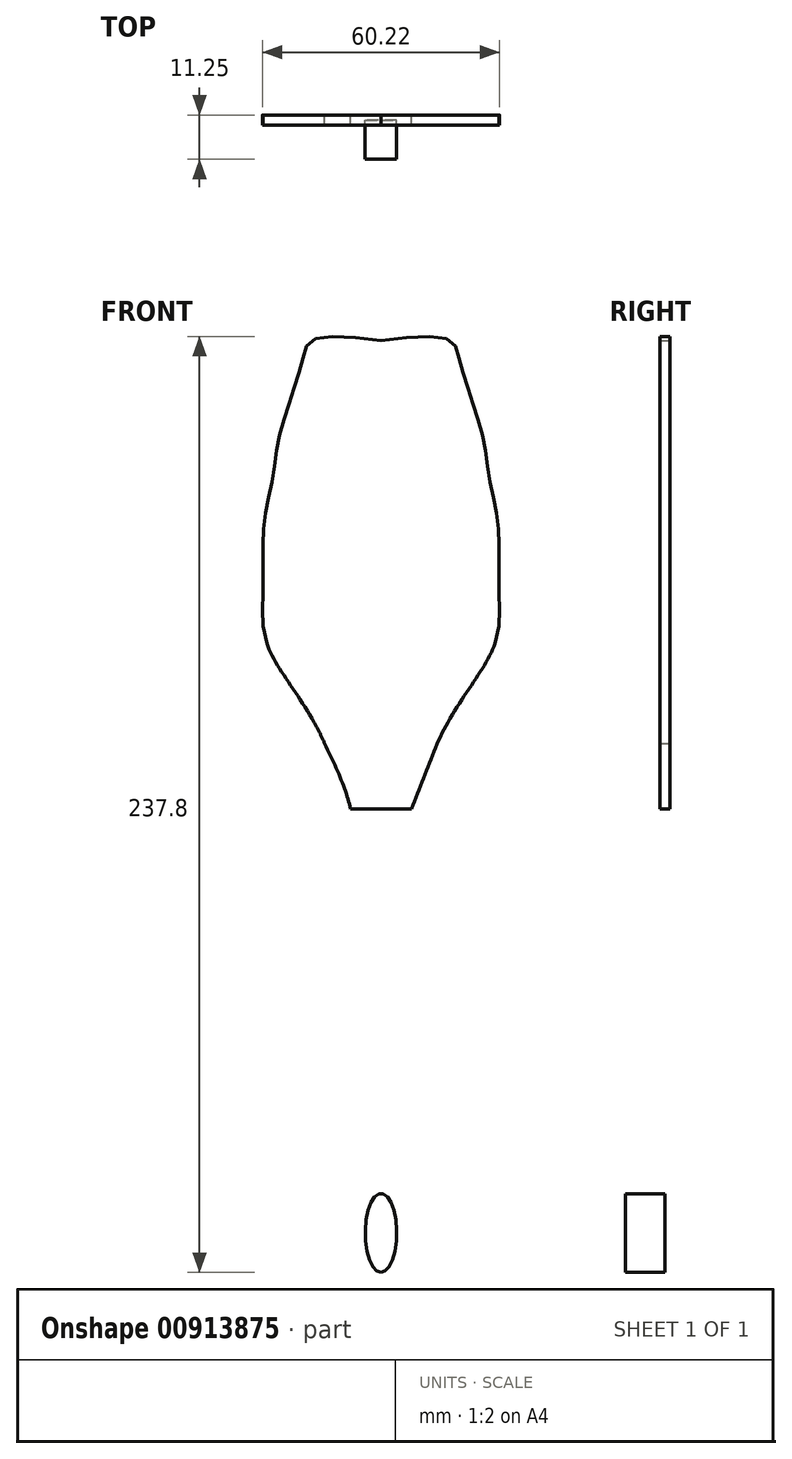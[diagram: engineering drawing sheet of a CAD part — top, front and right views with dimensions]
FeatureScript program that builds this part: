
annotation { "Feature Type Name" : "Feature", "Feature Type Description" : "" }
export const myFeature = defineFeature(function(context is Context, id is Id, definition is map)
    precondition{}
    {
        {
            var Q0;
            Q0=qCreatedBy(makeId("Front.planeOp"),FACE);
            var sketch = newSketch(context, id + "F0", { "sketchPlane" : qUnion([Q0])});
            skLineSegment(sketch, "E0", {"start": v(0, 0) * mm, "end": v(0, 20) * mm});
            skLineSegment(sketch, "E1", {"start": v(0, 20) * mm, "end": v(0, 22) * mm});
            skLineSegment(sketch, "E2", {"start": v(0, 22) * mm, "end": v(0, 32) * mm});
            skLineSegment(sketch, "E3", {"start": v(0, 32) * mm, "end": v(0, 42) * mm});
            skLineSegment(sketch, "E4", {"start": v(0, 42) * mm, "end": v(0, 52) * mm});
            skLineSegment(sketch, "E5", {"start": v(0, 52) * mm, "end": v(0, 62) * mm});
            skLineSegment(sketch, "E6", {"start": v(0, 62) * mm, "end": v(0, 72) * mm});
            skLineSegment(sketch, "E7", {"start": v(0, 72) * mm, "end": v(0, 82) * mm});
            skLineSegment(sketch, "E8", {"start": v(0, 82) * mm, "end": v(0, 92) * mm});
            skLineSegment(sketch, "E9", {"start": v(0, 92) * mm, "end": v(0, 97) * mm});
            skLineSegment(sketch, "E10", {"start": v(0, 20) * mm, "end": v(-29, 20) * mm, "construction": true});
            skLineSegment(sketch, "E11", {"start": v(0, 22) * mm, "end": v(-30, 22) * mm, "construction": true});
            skLineSegment(sketch, "E12", {"start": v(0, 32) * mm, "end": v(-30, 31.34) * mm, "construction": true});
            skLineSegment(sketch, "E13", {"start": v(0, 42) * mm, "end": v(-30, 42) * mm, "construction": true});
            skLineSegment(sketch, "E14", {"start": v(0, 52) * mm, "end": v(-29.5, 52) * mm, "construction": true});
            skLineSegment(sketch, "E15", {"start": v(0, 62) * mm, "end": v(-27.5, 62) * mm, "construction": true});
            skLineSegment(sketch, "E16", {"start": v(0, 72) * mm, "end": v(-26, 72) * mm, "construction": true});
            skLineSegment(sketch, "E17", {"start": v(0, 82) * mm, "end": v(-23, 82) * mm, "construction": true});
            skLineSegment(sketch, "E18", {"start": v(0, 92) * mm, "end": v(-20, 92) * mm, "construction": true});
            skLineSegment(sketch, "E19", {"start": v(0, 97) * mm, "end": v(-17.5, 97) * mm, "construction": true});
            skLineSegment(sketch, "E20", {"start": v(0, 0) * mm, "end": v(0, -22) * mm, "construction": true});
            skLineSegment(sketch, "E21", {"start": v(0, -22) * mm, "end": v(-7.75, -22) * mm});
            skLineSegment(sketch, "E22", {"start": v(0, -22) * mm, "end": v(0, -32) * mm, "construction": true});
            skLineSegment(sketch, "E23", {"start": v(0, -32) * mm, "end": v(0, -42) * mm, "construction": true});
            skLineSegment(sketch, "E24", {"start": v(0, -42) * mm, "end": v(0, -52) * mm, "construction": true});
            skLineSegment(sketch, "E25", {"start": v(0, -52) * mm, "end": v(0, -62) * mm, "construction": true});
            skLineSegment(sketch, "E26", {"start": v(0, -62) * mm, "end": v(0, -72) * mm, "construction": true});
            skLineSegment(sketch, "E27", {"start": v(0, -72) * mm, "end": v(0, -82) * mm, "construction": true});
            skLineSegment(sketch, "E28", {"start": v(0, -82) * mm, "end": v(0, -92) * mm, "construction": true});
            skLineSegment(sketch, "E29", {"start": v(0, -92) * mm, "end": v(0, -102) * mm, "construction": true});
            skLineSegment(sketch, "E30", {"start": v(0, -102) * mm, "end": v(0, -112) * mm, "construction": true});
            skLineSegment(sketch, "E31", {"start": v(0, -112) * mm, "end": v(0, -122) * mm, "construction": true});
            skLineSegment(sketch, "E32", {"start": v(0, -122) * mm, "end": v(0, -132) * mm, "construction": true});
            skLineSegment(sketch, "E33", {"start": v(0, -132) * mm, "end": v(0, -142) * mm, "construction": true});
            skLineSegment(sketch, "E34", {"start": v(0, -142) * mm, "end": v(0, -152) * mm, "construction": true});
            skLineSegment(sketch, "E35", {"start": v(0, -32) * mm, "end": v(-7.5, -32) * mm, "construction": true});
            skLineSegment(sketch, "E36", {"start": v(0, -42) * mm, "end": v(-7.6, -42) * mm, "construction": true});
            skLineSegment(sketch, "E37", {"start": v(0, -52) * mm, "end": v(-7.9, -52) * mm, "construction": true});
            skLineSegment(sketch, "E38", {"start": v(0, -62) * mm, "end": v(-8.4, -62) * mm, "construction": true});
            skLineSegment(sketch, "E39", {"start": v(0, -72) * mm, "end": v(-9, -72) * mm, "construction": true});
            skLineSegment(sketch, "E40", {"start": v(0, -82) * mm, "end": v(-10, -82) * mm, "construction": true});
            skLineSegment(sketch, "E41", {"start": v(0, -92) * mm, "end": v(-11, -92) * mm, "construction": true});
            skLineSegment(sketch, "E42", {"start": v(0, 0) * mm, "end": v(0, 10) * mm, "construction": true});
            skLineSegment(sketch, "E43", {"start": v(0, 10) * mm, "end": v(-23, 10) * mm});
            skLineSegment(sketch, "E44", {"start": v(0, 0) * mm, "end": v(0, 5) * mm, "construction": true});
            skLineSegment(sketch, "E45", {"start": v(0, 5) * mm, "end": v(-16.5, 5) * mm, "construction": true});
            skLineSegment(sketch, "E46", {"start": v(0, -102) * mm, "end": v(-11.5, -102) * mm, "construction": true});
            skLineSegment(sketch, "E47", {"start": v(0, -112) * mm, "end": v(-12, -112) * mm, "construction": true});
            skLineSegment(sketch, "E48", {"start": v(0, -122) * mm, "end": v(-12.2, -122) * mm, "construction": true});
            skLineSegment(sketch, "E49", {"start": v(0, -132) * mm, "end": v(-10.2, -132) * mm, "construction": true});
            skLineSegment(sketch, "E50", {"start": v(0, -142) * mm, "end": v(-7.5, -142) * mm, "construction": true});
            skLineSegment(sketch, "E51", {"start": v(0, -152) * mm, "end": v(-1.75, -152) * mm, "construction": true});
            skFitSpline(sketch, "E52", {"points": [v(0, -152) * mm, v(-1.75, -152) * mm, v(-7.5, -142) * mm, v(-10.2, -132) * mm, v(-12.2, -122) * mm, v(-12, -112) * mm, v(-11.5, -102) * mm, v(-11, -92) * mm, v(-10, -82) * mm, v(-9, -72) * mm, v(-8.4, -62) * mm, v(-7.9, -52) * mm, v(-7.6, -42) * mm, v(-7.5, -32) * mm, v(-7.75, -22) * mm, v(-17, 0) * mm], "startDerivative": vector(-58.6, -21.5) * mm, "endDerivative": vector(-117.56, 235.14) * mm});
            skFitSpline(sketch, "E53", {"points": [v(-17, 0) * mm, v(-29, 20) * mm, v(-30, 31.34) * mm, v(-30, 42) * mm, v(-29.5, 52) * mm, v(-27.5, 62) * mm, v(-26, 72) * mm, v(-23, 82) * mm, v(-20, 92) * mm, v(-17.5, 97) * mm, v(0, 97) * mm], "startDerivative": vector(-89.56, 159.99) * mm, "endDerivative": vector(177.3, -21.42) * mm});
            skFitSpline(sketch, "E54", {"points": [v(0, 0) * mm, v(-16.5, 5) * mm, v(-23, 10) * mm, v(-29, 20) * mm], "startDerivative": vector(-46.59, 11.68) * mm, "endDerivative": vector(-17.84, 33.73) * mm});
            skLineSegment(sketch, "E55", {"start": v(-17, 0) * mm, "end": v(0, 0) * mm});
            skFitSpline(sketch, "E56", {"points": [v(-17, 0) * mm, v(-7.75, -22) * mm], "startDerivative": vector(11.66, -20.82) * mm, "endDerivative": vector(9.25, -22) * mm});
            skLineSegment(sketch, "E57.MirrorCS", {"start": v(0, 5) * mm, "end": v(16.5, 5) * mm, "construction": true});
            skLineSegment(sketch, "E58.MirrorCS", {"start": v(0, 82) * mm, "end": v(23, 82) * mm, "construction": true});
            skLineSegment(sketch, "E59.MirrorCS", {"start": v(0, 42) * mm, "end": v(30, 42) * mm, "construction": true});
            skLineSegment(sketch, "E60.MirrorCS", {"start": v(0, 10) * mm, "end": v(23, 10) * mm});
            skLineSegment(sketch, "E61.MirrorCS", {"start": v(0, -22) * mm, "end": v(7.75, -22) * mm});
            skLineSegment(sketch, "E62.MirrorCS", {"start": v(0, 20) * mm, "end": v(29, 20) * mm, "construction": true});
            skFitSpline(sketch, "E63.MirrorCS", {"points": [v(0, 0) * mm, v(16.5, 5) * mm, v(23, 10) * mm, v(29, 20) * mm], "startDerivative": vector(46.59, 11.68) * mm, "endDerivative": vector(17.84, 33.73) * mm});
            skLineSegment(sketch, "E64.MirrorCS", {"start": v(0, 32) * mm, "end": v(30, 31.34) * mm, "construction": true});
            skFitSpline(sketch, "E65.MirrorCS", {"points": [v(17, 0) * mm, v(29, 20) * mm, v(30, 31.34) * mm, v(30, 42) * mm, v(29.5, 52) * mm, v(27.5, 62) * mm, v(26, 72) * mm, v(23, 82) * mm, v(20, 92) * mm, v(17.5, 97) * mm, v(0, 97) * mm], "startDerivative": vector(89.56, 159.99) * mm, "endDerivative": vector(-177.3, -21.42) * mm});
            skLineSegment(sketch, "E66.MirrorCS", {"start": v(0, 52) * mm, "end": v(29.5, 52) * mm, "construction": true});
            skLineSegment(sketch, "E67.MirrorCS", {"start": v(0, 72) * mm, "end": v(26, 72) * mm, "construction": true});
            skLineSegment(sketch, "E68.MirrorCS", {"start": v(17, 0) * mm, "end": v(0, 0) * mm});
            skLineSegment(sketch, "E69.MirrorCS", {"start": v(0, 62) * mm, "end": v(27.5, 62) * mm, "construction": true});
            skLineSegment(sketch, "E70.MirrorCS", {"start": v(0, 92) * mm, "end": v(20, 92) * mm, "construction": true});
            skLineSegment(sketch, "E71.MirrorCS", {"start": v(0, 22) * mm, "end": v(30, 22) * mm, "construction": true});
            skLineSegment(sketch, "E72.MirrorCS", {"start": v(0, 97) * mm, "end": v(17.5, 97) * mm, "construction": true});
            skFitSpline(sketch, "E73.MirrorCS", {"points": [v(17, 0) * mm, v(7.75, -22) * mm], "startDerivative": vector(-11.66, -20.82) * mm, "endDerivative": vector(-9.25, -22) * mm});
            skSolve(sketch);
        }
        {
            var Q0;
            Q0=qCreatedBy(makeId("Front.planeOp"),FACE);
            var sketch = newSketch(context, id + "F1", { "sketchPlane" : qUnion([Q0])});
            skFitSpline(sketch, "E74.0", {"points": [v(0, -152) * mm, v(-0.54, -152.2) * mm, v(-2.48, -152.9) * mm, v(-8.38, -141.33) * mm, v(-9.98, -132.26) * mm, v(-12.82, -122) * mm, v(-11.92, -112) * mm, v(-11.49, -102) * mm, v(-11.13, -91.99) * mm, v(-10, -82) * mm, v(-8.9, -72) * mm, v(-8.4, -62) * mm, v(-7.87, -51.99) * mm, v(-7.5, -42.06) * mm, v(-7.73, -31.76) * mm, v(-6.37, -21.27) * mm, v(-12.98, -8.03) * mm, v(-17, 0) * mm]});
            skLineSegment(sketch, "E75.0", {"start": v(0, 0) * mm, "end": v(0, -22) * mm});
            skLineSegment(sketch, "E76.0", {"start": v(0, -22) * mm, "end": v(0, -32) * mm});
            skLineSegment(sketch, "E77.0", {"start": v(0, -32) * mm, "end": v(0, -42) * mm});
            skLineSegment(sketch, "E78.0", {"start": v(0, -42) * mm, "end": v(0, -52) * mm});
            skLineSegment(sketch, "E79.0", {"start": v(0, -52) * mm, "end": v(0, -62) * mm});
            skPoint(sketch, "E80.0", {"position": v(0, -72) * mm});
            skLineSegment(sketch, "E81.0", {"start": v(0, -62) * mm, "end": v(0, -72) * mm});
            skLineSegment(sketch, "E82.0", {"start": v(0, -72) * mm, "end": v(0, -82) * mm});
            skLineSegment(sketch, "E83.0", {"start": v(0, -82) * mm, "end": v(0, -92) * mm});
            skPoint(sketch, "E84.0", {"position": v(0, -97) * mm});
            skLineSegment(sketch, "E85.0", {"start": v(0, -92) * mm, "end": v(0, -102) * mm});
            skPoint(sketch, "E86.0", {"position": v(0, -92) * mm});
            skPoint(sketch, "E87.0", {"position": v(0, -82) * mm});
            skPoint(sketch, "E88.0", {"position": v(0, -62) * mm});
            skPoint(sketch, "E89.0", {"position": v(0, -52) * mm});
            skPoint(sketch, "E90.0", {"position": v(0, -42) * mm});
            skPoint(sketch, "E91.0", {"position": v(0, -32) * mm});
            skPoint(sketch, "E92.0", {"position": v(0, -22) * mm});
            skPoint(sketch, "E93.0", {"position": v(-7.75, -22) * mm});
            skPoint(sketch, "E94.0", {"position": v(-7.5, -32) * mm});
            skPoint(sketch, "E95.0", {"position": v(-7.6, -42) * mm});
            skPoint(sketch, "E96.0", {"position": v(-7.9, -52) * mm});
            skPoint(sketch, "E97.0", {"position": v(-8.4, -62) * mm});
            skPoint(sketch, "E98.0", {"position": v(-9, -72) * mm});
            skPoint(sketch, "E99.0", {"position": v(-10, -82) * mm});
            skPoint(sketch, "E100.0", {"position": v(-11, -92) * mm});
            skPoint(sketch, "E101.0", {"position": v(-11.5, -102) * mm});
            skLineSegment(sketch, "E102.0", {"start": v(0, -102) * mm, "end": v(0, -112) * mm});
            skPoint(sketch, "E103.0", {"position": v(-12, -112) * mm});
            skPoint(sketch, "E104.0", {"position": v(0, -112) * mm});
            skPoint(sketch, "E105.0", {"position": v(-12.2, -122) * mm});
            skPoint(sketch, "E106.0", {"position": v(0, -122) * mm});
            skLineSegment(sketch, "E107.0", {"start": v(0, -112) * mm, "end": v(0, -122) * mm});
            skLineSegment(sketch, "E108.0", {"start": v(0, -122) * mm, "end": v(0, -132) * mm});
            skLineSegment(sketch, "E109.0", {"start": v(0, -132) * mm, "end": v(0, -142) * mm});
            skLineSegment(sketch, "E110.0", {"start": v(0, -142) * mm, "end": v(0, -152) * mm});
            skPoint(sketch, "E111.0", {"position": v(0, -152) * mm});
            skPoint(sketch, "E112.0", {"position": v(-1.75, -152) * mm});
            skPoint(sketch, "E113.0", {"position": v(-7.5, -142) * mm});
            skPoint(sketch, "E114.0", {"position": v(-10.2, -132) * mm});
            skPoint(sketch, "E115.0", {"position": v(0, -132) * mm});
            skPoint(sketch, "E116.0", {"position": v(0, -142) * mm});
            skSolve(sketch);
        }
        {
            var Q0;
            Q0 = qSketchRegion(id + "F1", true);
            var Q1;
            Q1=sQuery(id+"F1.wireOp",EDGE,"E74.0");
            var Q2;
            Q2=sQuery(id+"F1.wireOp",EDGE,"E75.0");
            revolve(context, id + "F2", {"bodyType" : ToolBodyType.SURFACE, "surfaceOperationType" : NewSurfaceOperationType.NEW, "entities" : qUnion([Q0]), "surfaceEntities" : qUnion([Q1]), "axis" : qUnion([Q2]), "revolveType" : RevolveType.FULL});
        }
        {
            var Q0;
            Q0=qCreatedBy(makeId("Front.planeOp"),FACE);
            var sketch = newSketch(context, id + "F3", { "sketchPlane" : qUnion([Q0])});
            skEllipse(sketch, "E117", {"center": v(0, -129.79) * mm, "majorRadius": 10 * mm, "minorRadius": 4 * mm, "majorAxis": v(0, -1)});
            skSolve(sketch);
        }
        {
            var Q0;
            Q0=makeQuery(id+"F3.imprint","IMPRINT",FACE,{"disambiguationData":[TD([[makeQuery(id+"F3.imprint","IMPRINT",EDGE,{"derivedFrom":sQuery(id+"F3.wireOp",EDGE,"E117")}),1.0]])]});
            extrude(context, id + "F4", {"entities" : qUnion([Q0]), "endBound" : BoundingType.SYMMETRIC, "depth" : 10 * mm, "offsetDistance" : 25 * mm});
        }
        {
            var Q0;
            Q0=makeQuery(id+"F0.imprint","IMPRINT",FACE,{"disambiguationData":[TD([[makeQuery(id+"F0.imprint","IMPRINT",EDGE,{"derivedFrom":sQuery(id+"F0.wireOp",EDGE,"E8")}),1.0]])]});
            var Q1;
            Q1=makeQuery(id+"F0.imprint","IMPRINT",FACE,{"disambiguationData":[TD([[makeQuery(id+"F0.imprint","IMPRINT",EDGE,{"derivedFrom":sQuery(id+"F0.wireOp",EDGE,"E8")}),-1.0]])]});
            var Q2;
            Q2=makeQuery(id+"F0.imprint","IMPRINT",FACE,{"disambiguationData":[TD([[makeQuery(id+"F0.imprint","IMPRINT",EDGE,{"derivedFrom":sQuery(id+"F0.wireOp",EDGE,"E21")}),-1.0]])]});
            var Q3;
            {var subQ0=sQuery(id+"F0.wireOp",EDGE,"E55");Q3=makeQuery(id+"F0.imprint","IMPRINT",FACE,{"disambiguationData":[TD([[makeQuery(id+"F0.imprint","IMPRINT",EDGE,{"derivedFrom":subQ0}),1.0]])]});}
            var Q4;
            {var subQ0=sQuery(id+"F0.wireOp",EDGE,"E68.MirrorCS");Q4=makeQuery(id+"F0.imprint","IMPRINT",FACE,{"disambiguationData":[TD([[makeQuery(id+"F0.imprint","IMPRINT",EDGE,{"derivedFrom":subQ0}),-1.0]])]});}
            var Q5;
            {var subQ0=sQuery(id+"F0.wireOp",EDGE,"E60.MirrorCS");Q5=makeQuery(id+"F0.imprint","IMPRINT",FACE,{"disambiguationData":[TD([[makeQuery(id+"F0.imprint","IMPRINT",EDGE,{"derivedFrom":subQ0}),-1.0]])]});}
            var Q6;
            {var subQ0=sQuery(id+"F0.wireOp",EDGE,"E43");Q6=makeQuery(id+"F0.imprint","IMPRINT",FACE,{"disambiguationData":[TD([[makeQuery(id+"F0.imprint","IMPRINT",EDGE,{"derivedFrom":subQ0}),1.0]])]});}
            extrude(context, id + "F5", {"entities" : qUnion([Q0, Q1, Q2, Q3, Q4, Q5, Q6]), "endBound" : BoundingType.SYMMETRIC, "depth" : 12.5 * mm, "offsetDistance" : 25 * mm});
        }
        {
            var Q0;
            Q0=makeQuery(id+"F5.opExtrude","CAP_FACE",FACE,{"disambiguationData":[OSD([sQuery(id+"F0.wireOp",EDGE,"E21"),sQuery(id+"F0.wireOp",EDGE,"E53"),sQuery(id+"F0.wireOp",EDGE,"E56"),sQuery(id+"F0.wireOp",EDGE,"E61.MirrorCS"),sQuery(id+"F0.wireOp",EDGE,"E65.MirrorCS"),sQuery(id+"F0.wireOp",EDGE,"E73.MirrorCS")])],"isStart":false});
            extrude(context, id + "F6", {"entities" : qUnion([Q0]), "operationType" : NewBodyOperationType.REMOVE, "oppositeDirection" : true, "depth" : 10 * mm, "offsetDistance" : 25 * mm});
        }
    });
